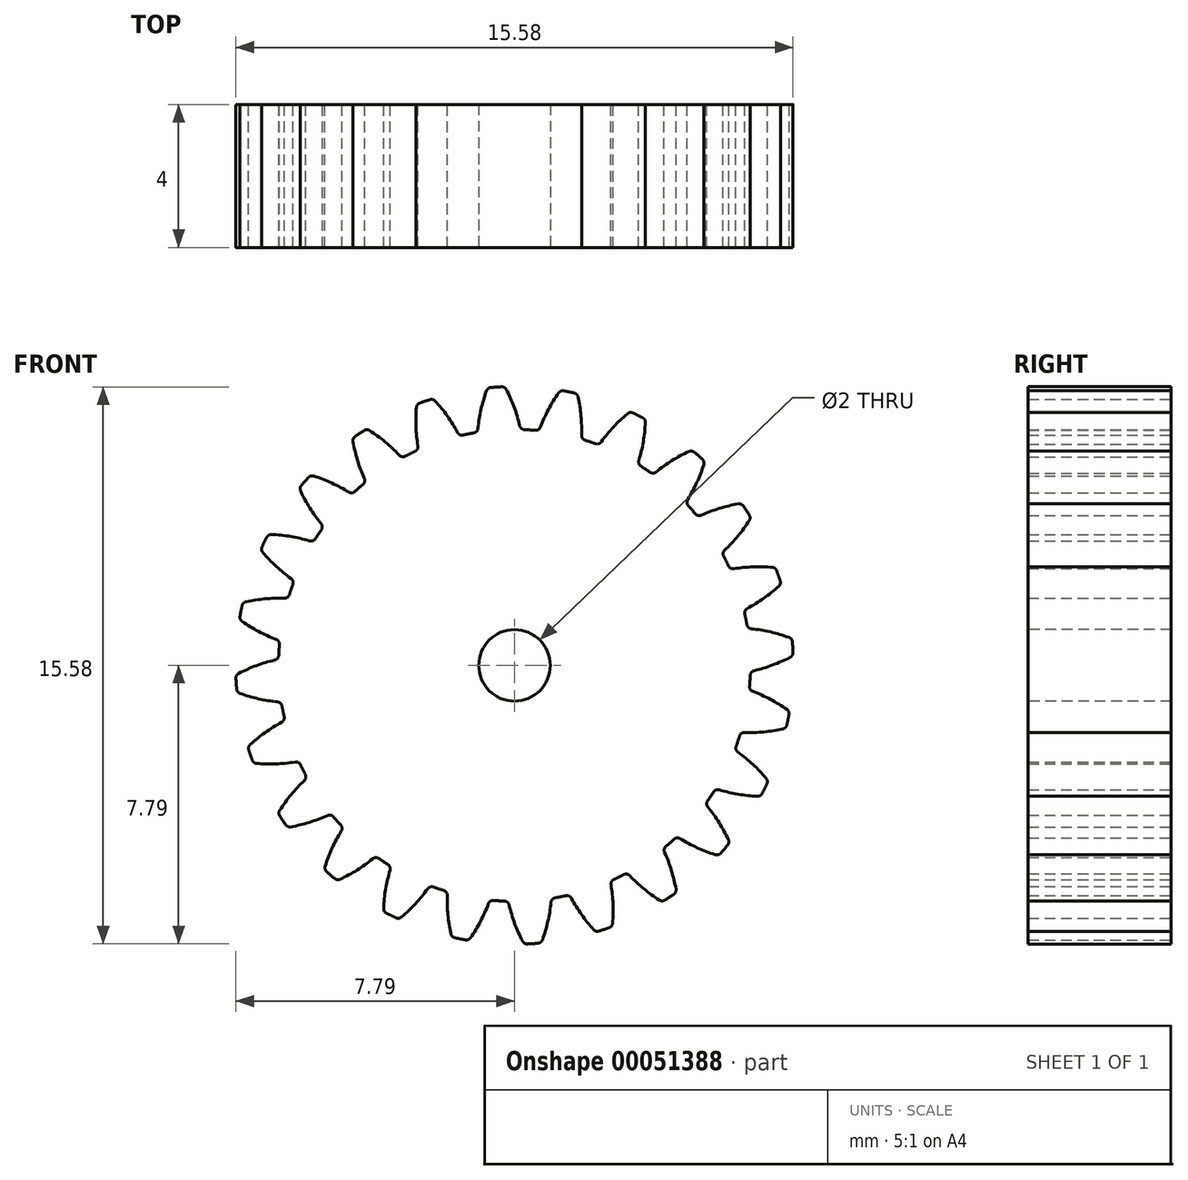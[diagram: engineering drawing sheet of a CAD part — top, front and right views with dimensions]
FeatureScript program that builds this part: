
annotation { "Feature Type Name" : "Feature", "Feature Type Description" : "" }
export const myFeature = defineFeature(function(context is Context, id is Id, definition is map)
    precondition{}
    {
        {
            var Q0;
            Q0=qCreatedBy(makeId("Front.planeOp"),FACE);
            var sketch = newSketch(context, id + "F0", { "sketchPlane" : qUnion([Q0])});
            skCircle(sketch, "E0", {"center": v(0, 0) * mm, "radius": 6.6 * mm, "construction": true});
            skCircle(sketch, "E1", {"center": v(0, 0) * mm, "radius": 7.2 * mm, "construction": true});
            skCircle(sketch, "E2", {"center": v(0, 0) * mm, "radius": 7.8 * mm, "construction": true});
            skLineSegment(sketch, "E3", {"start": v(0, 0) * mm, "end": v(0, 6.31) * mm, "construction": true});
            skCircle(sketch, "E4", {"center": v(0, 7.2) * mm, "radius": 4.32 * mm, "construction": true});
            skCircle(sketch, "E5.cCircle", {"center": v(0, 0) * mm, "radius": 6.31 * mm, "construction": true});
            skLineSegment(sketch, "E5.0", {"start": v(0, 6.31) * mm, "end": v(0.82, 6.26) * mm, "construction": true});
            skLineSegment(sketch, "E5.1", {"start": v(0.82, 6.26) * mm, "end": v(1.63, 6.1) * mm, "construction": true});
            skLineSegment(sketch, "E5.2", {"start": v(1.63, 6.1) * mm, "end": v(2.41, 5.83) * mm, "construction": true});
            skLineSegment(sketch, "E5.3", {"start": v(2.41, 5.83) * mm, "end": v(3.16, 5.46) * mm, "construction": true});
            skLineSegment(sketch, "E5.4", {"start": v(3.16, 5.46) * mm, "end": v(3.84, 5) * mm, "construction": true});
            skLineSegment(sketch, "E5.5", {"start": v(3.84, 5) * mm, "end": v(4.46, 4.46) * mm, "construction": true});
            skLineSegment(sketch, "E5.6", {"start": v(4.46, 4.46) * mm, "end": v(5, 3.84) * mm, "construction": true});
            skLineSegment(sketch, "E5.7", {"start": v(5, 3.84) * mm, "end": v(5.46, 3.16) * mm, "construction": true});
            skLineSegment(sketch, "E5.8", {"start": v(5.46, 3.16) * mm, "end": v(5.83, 2.41) * mm, "construction": true});
            skLineSegment(sketch, "E5.9", {"start": v(5.83, 2.41) * mm, "end": v(6.1, 1.63) * mm, "construction": true});
            skLineSegment(sketch, "E5.10", {"start": v(6.1, 1.63) * mm, "end": v(6.26, 0.82) * mm, "construction": true});
            skLineSegment(sketch, "E5.11", {"start": v(6.26, 0.82) * mm, "end": v(6.31, 0) * mm, "construction": true});
            skLineSegment(sketch, "E5.12", {"start": v(6.31, 0) * mm, "end": v(6.26, -0.82) * mm, "construction": true});
            skLineSegment(sketch, "E5.13", {"start": v(6.26, -0.82) * mm, "end": v(6.1, -1.63) * mm, "construction": true});
            skLineSegment(sketch, "E5.14", {"start": v(6.1, -1.63) * mm, "end": v(5.83, -2.41) * mm, "construction": true});
            skLineSegment(sketch, "E5.15", {"start": v(5.83, -2.41) * mm, "end": v(5.46, -3.16) * mm, "construction": true});
            skLineSegment(sketch, "E5.16", {"start": v(5.46, -3.16) * mm, "end": v(5, -3.84) * mm, "construction": true});
            skLineSegment(sketch, "E5.17", {"start": v(5, -3.84) * mm, "end": v(4.46, -4.46) * mm, "construction": true});
            skLineSegment(sketch, "E5.18", {"start": v(4.46, -4.46) * mm, "end": v(3.84, -5) * mm, "construction": true});
            skLineSegment(sketch, "E5.19", {"start": v(3.84, -5) * mm, "end": v(3.16, -5.46) * mm, "construction": true});
            skLineSegment(sketch, "E5.20", {"start": v(3.16, -5.46) * mm, "end": v(2.41, -5.83) * mm, "construction": true});
            skLineSegment(sketch, "E5.21", {"start": v(2.41, -5.83) * mm, "end": v(1.63, -6.1) * mm, "construction": true});
            skLineSegment(sketch, "E5.22", {"start": v(1.63, -6.1) * mm, "end": v(0.82, -6.26) * mm, "construction": true});
            skLineSegment(sketch, "E5.23", {"start": v(0.82, -6.26) * mm, "end": v(0, -6.31) * mm, "construction": true});
            skLineSegment(sketch, "E5.24", {"start": v(0, -6.31) * mm, "end": v(-0.82, -6.26) * mm, "construction": true});
            skLineSegment(sketch, "E5.25", {"start": v(-0.82, -6.26) * mm, "end": v(-1.63, -6.1) * mm, "construction": true});
            skLineSegment(sketch, "E5.26", {"start": v(-1.63, -6.1) * mm, "end": v(-2.41, -5.83) * mm, "construction": true});
            skLineSegment(sketch, "E5.27", {"start": v(-2.41, -5.83) * mm, "end": v(-3.16, -5.46) * mm, "construction": true});
            skLineSegment(sketch, "E5.28", {"start": v(-3.16, -5.46) * mm, "end": v(-3.84, -5) * mm, "construction": true});
            skLineSegment(sketch, "E5.29", {"start": v(-3.84, -5) * mm, "end": v(-4.46, -4.46) * mm, "construction": true});
            skLineSegment(sketch, "E5.30", {"start": v(-4.46, -4.46) * mm, "end": v(-5, -3.84) * mm, "construction": true});
            skLineSegment(sketch, "E5.31", {"start": v(-5, -3.84) * mm, "end": v(-5.46, -3.16) * mm, "construction": true});
            skLineSegment(sketch, "E5.32", {"start": v(-5.46, -3.16) * mm, "end": v(-5.83, -2.41) * mm, "construction": true});
            skLineSegment(sketch, "E5.33", {"start": v(-5.83, -2.41) * mm, "end": v(-6.1, -1.63) * mm, "construction": true});
            skLineSegment(sketch, "E5.34", {"start": v(-6.1, -1.63) * mm, "end": v(-6.26, -0.82) * mm, "construction": true});
            skLineSegment(sketch, "E5.35", {"start": v(-6.26, -0.82) * mm, "end": v(-6.31, 0) * mm, "construction": true});
            skLineSegment(sketch, "E5.36", {"start": v(-6.31, 0) * mm, "end": v(-6.26, 0.82) * mm, "construction": true});
            skLineSegment(sketch, "E5.37", {"start": v(-6.26, 0.82) * mm, "end": v(-6.1, 1.63) * mm, "construction": true});
            skLineSegment(sketch, "E5.38", {"start": v(-6.1, 1.63) * mm, "end": v(-5.83, 2.41) * mm, "construction": true});
            skLineSegment(sketch, "E5.39", {"start": v(-5.83, 2.41) * mm, "end": v(-5.46, 3.16) * mm, "construction": true});
            skLineSegment(sketch, "E5.40", {"start": v(-5.46, 3.16) * mm, "end": v(-5, 3.84) * mm, "construction": true});
            skLineSegment(sketch, "E5.41", {"start": v(-5, 3.84) * mm, "end": v(-4.46, 4.46) * mm, "construction": true});
            skLineSegment(sketch, "E5.42", {"start": v(-4.46, 4.46) * mm, "end": v(-3.84, 5) * mm, "construction": true});
            skLineSegment(sketch, "E5.43", {"start": v(-3.84, 5) * mm, "end": v(-3.16, 5.46) * mm, "construction": true});
            skLineSegment(sketch, "E5.44", {"start": v(-3.16, 5.46) * mm, "end": v(-2.41, 5.83) * mm, "construction": true});
            skLineSegment(sketch, "E5.45", {"start": v(-2.41, 5.83) * mm, "end": v(-1.63, 6.1) * mm, "construction": true});
            skLineSegment(sketch, "E5.46", {"start": v(-1.63, 6.1) * mm, "end": v(-0.82, 6.26) * mm, "construction": true});
            skLineSegment(sketch, "E5.47", {"start": v(-0.82, 6.26) * mm, "end": v(0, 6.31) * mm, "construction": true});
            skLineSegment(sketch, "E6.0", {"start": v(-0.41, 6.31) * mm, "end": v(0.41, 6.31) * mm});
            skLineSegment(sketch, "E6.1", {"start": v(0.41, 6.31) * mm, "end": v(1.23, 6.2) * mm});
            skLineSegment(sketch, "E6.2", {"start": v(1.23, 6.2) * mm, "end": v(2.03, 5.99) * mm});
            skLineSegment(sketch, "E6.3", {"start": v(2.03, 5.99) * mm, "end": v(2.8, 5.67) * mm});
            skLineSegment(sketch, "E6.4", {"start": v(2.8, 5.67) * mm, "end": v(3.51, 5.26) * mm});
            skLineSegment(sketch, "E6.5", {"start": v(3.51, 5.26) * mm, "end": v(4.17, 4.75) * mm});
            skLineSegment(sketch, "E6.6", {"start": v(4.17, 4.75) * mm, "end": v(4.75, 4.17) * mm});
            skLineSegment(sketch, "E6.7", {"start": v(4.75, 4.17) * mm, "end": v(5.26, 3.51) * mm, "construction": true});
            skLineSegment(sketch, "E6.8", {"start": v(5.26, 3.51) * mm, "end": v(5.67, 2.8) * mm});
            skLineSegment(sketch, "E6.9", {"start": v(5.67, 2.8) * mm, "end": v(5.99, 2.03) * mm});
            skLineSegment(sketch, "E6.10", {"start": v(5.99, 2.03) * mm, "end": v(6.2, 1.23) * mm});
            skLineSegment(sketch, "E6.11", {"start": v(6.2, 1.23) * mm, "end": v(6.31, 0.41) * mm});
            skLineSegment(sketch, "E6.12", {"start": v(6.31, 0.41) * mm, "end": v(6.31, -0.41) * mm});
            skLineSegment(sketch, "E6.13", {"start": v(6.31, -0.41) * mm, "end": v(6.2, -1.23) * mm});
            skLineSegment(sketch, "E6.14", {"start": v(6.2, -1.23) * mm, "end": v(5.99, -2.03) * mm});
            skLineSegment(sketch, "E6.15", {"start": v(5.99, -2.03) * mm, "end": v(5.67, -2.8) * mm});
            skLineSegment(sketch, "E6.16", {"start": v(5.67, -2.8) * mm, "end": v(5.26, -3.51) * mm});
            skLineSegment(sketch, "E6.17", {"start": v(5.26, -3.51) * mm, "end": v(4.75, -4.17) * mm});
            skLineSegment(sketch, "E6.18", {"start": v(4.75, -4.17) * mm, "end": v(4.17, -4.75) * mm});
            skLineSegment(sketch, "E6.19", {"start": v(4.17, -4.75) * mm, "end": v(3.51, -5.26) * mm});
            skLineSegment(sketch, "E6.20", {"start": v(3.51, -5.26) * mm, "end": v(2.8, -5.67) * mm});
            skLineSegment(sketch, "E6.21", {"start": v(2.8, -5.67) * mm, "end": v(2.03, -5.99) * mm});
            skLineSegment(sketch, "E6.22", {"start": v(2.03, -5.99) * mm, "end": v(1.23, -6.2) * mm});
            skLineSegment(sketch, "E6.23", {"start": v(1.23, -6.2) * mm, "end": v(0.41, -6.31) * mm});
            skLineSegment(sketch, "E6.24", {"start": v(0.41, -6.31) * mm, "end": v(-0.41, -6.31) * mm});
            skLineSegment(sketch, "E6.25", {"start": v(-0.41, -6.31) * mm, "end": v(-1.23, -6.2) * mm});
            skLineSegment(sketch, "E6.26", {"start": v(-1.23, -6.2) * mm, "end": v(-2.03, -5.99) * mm});
            skLineSegment(sketch, "E6.27", {"start": v(-2.03, -5.99) * mm, "end": v(-2.8, -5.67) * mm});
            skLineSegment(sketch, "E6.28", {"start": v(-2.8, -5.67) * mm, "end": v(-3.51, -5.26) * mm});
            skLineSegment(sketch, "E6.29", {"start": v(-3.51, -5.26) * mm, "end": v(-4.17, -4.75) * mm});
            skLineSegment(sketch, "E6.30", {"start": v(-4.17, -4.75) * mm, "end": v(-4.75, -4.17) * mm});
            skLineSegment(sketch, "E6.31", {"start": v(-4.75, -4.17) * mm, "end": v(-5.26, -3.51) * mm});
            skLineSegment(sketch, "E6.32", {"start": v(-5.26, -3.51) * mm, "end": v(-5.67, -2.8) * mm});
            skLineSegment(sketch, "E6.33", {"start": v(-5.67, -2.8) * mm, "end": v(-5.99, -2.03) * mm});
            skLineSegment(sketch, "E6.34", {"start": v(-5.99, -2.03) * mm, "end": v(-6.2, -1.23) * mm});
            skLineSegment(sketch, "E6.35", {"start": v(-6.2, -1.23) * mm, "end": v(-6.31, -0.41) * mm});
            skLineSegment(sketch, "E6.36", {"start": v(-6.31, -0.41) * mm, "end": v(-6.31, 0.41) * mm});
            skLineSegment(sketch, "E6.37", {"start": v(-6.31, 0.41) * mm, "end": v(-6.2, 1.23) * mm});
            skLineSegment(sketch, "E6.38", {"start": v(-6.2, 1.23) * mm, "end": v(-5.99, 2.03) * mm});
            skLineSegment(sketch, "E6.39", {"start": v(-5.99, 2.03) * mm, "end": v(-5.67, 2.8) * mm});
            skLineSegment(sketch, "E6.40", {"start": v(-5.67, 2.8) * mm, "end": v(-5.26, 3.51) * mm});
            skLineSegment(sketch, "E6.41", {"start": v(-5.26, 3.51) * mm, "end": v(-4.75, 4.17) * mm});
            skLineSegment(sketch, "E6.42", {"start": v(-4.75, 4.17) * mm, "end": v(-4.17, 4.75) * mm});
            skLineSegment(sketch, "E6.43", {"start": v(-4.17, 4.75) * mm, "end": v(-3.51, 5.26) * mm});
            skLineSegment(sketch, "E6.44", {"start": v(-3.51, 5.26) * mm, "end": v(-2.8, 5.67) * mm});
            skLineSegment(sketch, "E6.45", {"start": v(-2.8, 5.67) * mm, "end": v(-2.03, 5.99) * mm});
            skLineSegment(sketch, "E6.46", {"start": v(-2.03, 5.99) * mm, "end": v(-1.23, 6.2) * mm});
            skLineSegment(sketch, "E6.47", {"start": v(-1.23, 6.2) * mm, "end": v(-0.41, 6.31) * mm});
            skPoint(sketch, "E6.0.midPoint", {"position": v(0, 6.31) * mm});
            skLineSegment(sketch, "E7", {"start": v(0, 7.2) * mm, "end": v(-9.03, 7.2) * mm, "construction": true});
            skLineSegment(sketch, "E8", {"start": v(0, 7.2) * mm, "end": v(-8.97, 3.93) * mm, "construction": true});
            skCircle(sketch, "E9", {"center": v(-4.06, 5.72) * mm, "radius": 4.32 * mm, "construction": true});
            skArc(sketch, "E10", {"start": v(-0.23, 7.71) * mm, "mid": v(0, 7.22) * mm, "end": v(0.15, 6.7) * mm});
            skLineSegment(sketch, "E11", {"start": v(0, 0) * mm, "end": v(-0.41, 6.31) * mm, "construction": true});
            skArc(sketch, "E12.MirrorCS", {"start": v(-0.78, 7.68) * mm, "mid": v(-0.93, 7.16) * mm, "end": v(-1.02, 6.63) * mm});
            skArc(sketch, "E13", {"start": v(-0.66, 7.77) * mm, "mid": v(-0.51, 7.78) * mm, "end": v(-0.36, 7.8) * mm});
            skArc(sketch, "E14", {"start": v(-1.14, 6.5) * mm, "mid": v(0.43, -6.59) * mm, "end": v(0.28, 6.6) * mm});
            skPoint(sketch, "E15.visualSharp", {"position": v(-1.03, 6.52) * mm});
            skArc(sketch, "E15.filletArc", {"start": v(-1.14, 6.5) * mm, "mid": v(-1.06, 6.54) * mm, "end": v(-1.02, 6.63) * mm});
            skPoint(sketch, "E16.visualSharp", {"position": v(0.17, 6.6) * mm});
            skArc(sketch, "E16.filletArc", {"start": v(0.15, 6.7) * mm, "mid": v(0.2, 6.63) * mm, "end": v(0.28, 6.6) * mm});
            skPoint(sketch, "E17.visualSharp", {"position": v(-0.75, 7.76) * mm});
            skArc(sketch, "E17.filletArc", {"start": v(-0.66, 7.77) * mm, "mid": v(-0.74, 7.74) * mm, "end": v(-0.78, 7.68) * mm});
            skPoint(sketch, "E18.visualSharp", {"position": v(-0.27, 7.8) * mm});
            skArc(sketch, "E18.filletArc", {"start": v(-0.23, 7.71) * mm, "mid": v(-0.28, 7.77) * mm, "end": v(-0.36, 7.8) * mm});
            skArc(sketch, "E19.1.0", {"start": v(-2.78, 5.98) * mm, "mid": v(-2.72, 6.05) * mm, "end": v(-2.7, 6.14) * mm});
            skArc(sketch, "E19.1.1", {"start": v(-2.74, 7.21) * mm, "mid": v(-2.76, 6.67) * mm, "end": v(-2.7, 6.14) * mm});
            skArc(sketch, "E19.1.2", {"start": v(-2.65, 7.34) * mm, "mid": v(-2.71, 7.29) * mm, "end": v(-2.74, 7.21) * mm});
            skArc(sketch, "E19.1.3", {"start": v(-2.65, 7.34) * mm, "mid": v(-2.5, 7.39) * mm, "end": v(-2.36, 7.43) * mm});
            skArc(sketch, "E19.1.4", {"start": v(-2.21, 7.4) * mm, "mid": v(-2.28, 7.43) * mm, "end": v(-2.36, 7.43) * mm});
            skArc(sketch, "E19.1.5", {"start": v(-2.21, 7.4) * mm, "mid": v(-1.88, 6.97) * mm, "end": v(-1.6, 6.51) * mm});
            skArc(sketch, "E19.1.6", {"start": v(-1.6, 6.51) * mm, "mid": v(-1.53, 6.45) * mm, "end": v(-1.43, 6.44) * mm});
            skArc(sketch, "E19.2.0", {"start": v(-4.24, 5.06) * mm, "mid": v(-4.19, 5.14) * mm, "end": v(-4.2, 5.23) * mm});
            skArc(sketch, "E19.2.1", {"start": v(-4.52, 6.26) * mm, "mid": v(-4.39, 5.73) * mm, "end": v(-4.2, 5.23) * mm});
            skArc(sketch, "E19.2.2", {"start": v(-4.46, 6.4) * mm, "mid": v(-4.5, 6.34) * mm, "end": v(-4.52, 6.26) * mm});
            skArc(sketch, "E19.2.3", {"start": v(-4.46, 6.4) * mm, "mid": v(-4.33, 6.49) * mm, "end": v(-4.2, 6.57) * mm});
            skArc(sketch, "E19.2.4", {"start": v(-4.05, 6.57) * mm, "mid": v(-4.13, 6.6) * mm, "end": v(-4.2, 6.57) * mm});
            skArc(sketch, "E19.2.5", {"start": v(-4.05, 6.57) * mm, "mid": v(-3.62, 6.25) * mm, "end": v(-3.23, 5.88) * mm});
            skArc(sketch, "E19.2.6", {"start": v(-3.23, 5.88) * mm, "mid": v(-3.14, 5.84) * mm, "end": v(-3.05, 5.85) * mm});
            skArc(sketch, "E19.3.0", {"start": v(-5.4, 3.8) * mm, "mid": v(-5.38, 3.88) * mm, "end": v(-5.4, 3.96) * mm});
            skArc(sketch, "E19.3.1", {"start": v(-5.98, 4.88) * mm, "mid": v(-5.72, 4.4) * mm, "end": v(-5.4, 3.96) * mm});
            skArc(sketch, "E19.3.2", {"start": v(-5.96, 5.03) * mm, "mid": v(-6, 4.96) * mm, "end": v(-5.98, 4.88) * mm});
            skArc(sketch, "E19.3.3", {"start": v(-5.96, 5.03) * mm, "mid": v(-5.86, 5.14) * mm, "end": v(-5.76, 5.25) * mm});
            skArc(sketch, "E19.3.4", {"start": v(-5.61, 5.3) * mm, "mid": v(-5.7, 5.3) * mm, "end": v(-5.76, 5.25) * mm});
            skArc(sketch, "E19.3.5", {"start": v(-5.61, 5.3) * mm, "mid": v(-5.11, 5.1) * mm, "end": v(-4.64, 4.85) * mm});
            skArc(sketch, "E19.3.6", {"start": v(-4.64, 4.85) * mm, "mid": v(-4.55, 4.82) * mm, "end": v(-4.46, 4.86) * mm});
            skArc(sketch, "E19.4.0", {"start": v(-6.2, 2.26) * mm, "mid": v(-6.2, 2.36) * mm, "end": v(-6.25, 2.43) * mm});
            skArc(sketch, "E19.4.1", {"start": v(-7.04, 3.16) * mm, "mid": v(-6.67, 2.77) * mm, "end": v(-6.25, 2.43) * mm});
            skArc(sketch, "E19.4.2", {"start": v(-7.06, 3.31) * mm, "mid": v(-7.07, 3.23) * mm, "end": v(-7.04, 3.16) * mm});
            skArc(sketch, "E19.4.3", {"start": v(-7.06, 3.31) * mm, "mid": v(-7, 3.45) * mm, "end": v(-6.93, 3.58) * mm});
            skArc(sketch, "E19.4.4", {"start": v(-6.8, 3.66) * mm, "mid": v(-6.87, 3.64) * mm, "end": v(-6.93, 3.58) * mm});
            skArc(sketch, "E19.4.5", {"start": v(-6.8, 3.66) * mm, "mid": v(-6.26, 3.6) * mm, "end": v(-5.73, 3.48) * mm});
            skArc(sketch, "E19.4.6", {"start": v(-5.73, 3.48) * mm, "mid": v(-5.64, 3.48) * mm, "end": v(-5.57, 3.54) * mm});
            skArc(sketch, "E19.5.0", {"start": v(-6.57, 0.58) * mm, "mid": v(-6.6, 0.67) * mm, "end": v(-6.67, 0.73) * mm});
            skArc(sketch, "E19.5.1", {"start": v(-7.62, 1.23) * mm, "mid": v(-7.16, 0.95) * mm, "end": v(-6.67, 0.73) * mm});
            skArc(sketch, "E19.5.2", {"start": v(-7.68, 1.37) * mm, "mid": v(-7.67, 1.3) * mm, "end": v(-7.62, 1.23) * mm});
            skArc(sketch, "E19.5.3", {"start": v(-7.68, 1.37) * mm, "mid": v(-7.65, 1.52) * mm, "end": v(-7.62, 1.67) * mm});
            skArc(sketch, "E19.5.4", {"start": v(-7.5, 1.78) * mm, "mid": v(-7.58, 1.74) * mm, "end": v(-7.62, 1.67) * mm});
            skArc(sketch, "E19.5.5", {"start": v(-7.5, 1.78) * mm, "mid": v(-6.98, 1.86) * mm, "end": v(-6.44, 1.88) * mm});
            skArc(sketch, "E19.5.6", {"start": v(-6.44, 1.88) * mm, "mid": v(-6.35, 1.9) * mm, "end": v(-6.3, 1.98) * mm});
            skArc(sketch, "E19.6.0", {"start": v(-6.5, -1.14) * mm, "mid": v(-6.54, -1.06) * mm, "end": v(-6.63, -1.02) * mm});
            skArc(sketch, "E19.6.1", {"start": v(-7.68, -0.78) * mm, "mid": v(-7.16, -0.93) * mm, "end": v(-6.63, -1.02) * mm});
            skArc(sketch, "E19.6.2", {"start": v(-7.77, -0.66) * mm, "mid": v(-7.74, -0.74) * mm, "end": v(-7.68, -0.78) * mm});
            skArc(sketch, "E19.6.3", {"start": v(-7.77, -0.66) * mm, "mid": v(-7.78, -0.51) * mm, "end": v(-7.8, -0.36) * mm});
            skArc(sketch, "E19.6.4", {"start": v(-7.71, -0.23) * mm, "mid": v(-7.77, -0.28) * mm, "end": v(-7.8, -0.36) * mm});
            skArc(sketch, "E19.6.5", {"start": v(-7.71, -0.23) * mm, "mid": v(-7.22, 0) * mm, "end": v(-6.7, 0.15) * mm});
            skArc(sketch, "E19.6.6", {"start": v(-6.7, 0.15) * mm, "mid": v(-6.63, 0.2) * mm, "end": v(-6.6, 0.28) * mm});
            skArc(sketch, "E19.7.0", {"start": v(-5.98, -2.78) * mm, "mid": v(-6.05, -2.72) * mm, "end": v(-6.14, -2.7) * mm});
            skArc(sketch, "E19.7.1", {"start": v(-7.21, -2.74) * mm, "mid": v(-6.67, -2.76) * mm, "end": v(-6.14, -2.7) * mm});
            skArc(sketch, "E19.7.2", {"start": v(-7.34, -2.65) * mm, "mid": v(-7.29, -2.71) * mm, "end": v(-7.21, -2.74) * mm});
            skArc(sketch, "E19.7.3", {"start": v(-7.34, -2.65) * mm, "mid": v(-7.39, -2.5) * mm, "end": v(-7.43, -2.36) * mm});
            skArc(sketch, "E19.7.4", {"start": v(-7.4, -2.21) * mm, "mid": v(-7.43, -2.28) * mm, "end": v(-7.43, -2.36) * mm});
            skArc(sketch, "E19.7.5", {"start": v(-7.4, -2.21) * mm, "mid": v(-6.97, -1.88) * mm, "end": v(-6.51, -1.6) * mm});
            skArc(sketch, "E19.7.6", {"start": v(-6.51, -1.6) * mm, "mid": v(-6.45, -1.53) * mm, "end": v(-6.44, -1.43) * mm});
            skArc(sketch, "E19.8.0", {"start": v(-5.06, -4.24) * mm, "mid": v(-5.14, -4.19) * mm, "end": v(-5.23, -4.2) * mm});
            skArc(sketch, "E19.8.1", {"start": v(-6.26, -4.52) * mm, "mid": v(-5.73, -4.39) * mm, "end": v(-5.23, -4.2) * mm});
            skArc(sketch, "E19.8.2", {"start": v(-6.4, -4.46) * mm, "mid": v(-6.34, -4.5) * mm, "end": v(-6.26, -4.52) * mm});
            skArc(sketch, "E19.8.3", {"start": v(-6.4, -4.46) * mm, "mid": v(-6.49, -4.33) * mm, "end": v(-6.57, -4.2) * mm});
            skArc(sketch, "E19.8.4", {"start": v(-6.57, -4.05) * mm, "mid": v(-6.6, -4.13) * mm, "end": v(-6.57, -4.2) * mm});
            skArc(sketch, "E19.8.5", {"start": v(-6.57, -4.05) * mm, "mid": v(-6.25, -3.62) * mm, "end": v(-5.88, -3.23) * mm});
            skArc(sketch, "E19.8.6", {"start": v(-5.88, -3.23) * mm, "mid": v(-5.84, -3.14) * mm, "end": v(-5.85, -3.05) * mm});
            skArc(sketch, "E19.9.0", {"start": v(-3.8, -5.4) * mm, "mid": v(-3.88, -5.38) * mm, "end": v(-3.96, -5.4) * mm});
            skArc(sketch, "E19.9.1", {"start": v(-4.88, -5.98) * mm, "mid": v(-4.4, -5.72) * mm, "end": v(-3.96, -5.4) * mm});
            skArc(sketch, "E19.9.2", {"start": v(-5.03, -5.96) * mm, "mid": v(-4.96, -6) * mm, "end": v(-4.88, -5.98) * mm});
            skArc(sketch, "E19.9.3", {"start": v(-5.03, -5.96) * mm, "mid": v(-5.14, -5.86) * mm, "end": v(-5.25, -5.76) * mm});
            skArc(sketch, "E19.9.4", {"start": v(-5.3, -5.61) * mm, "mid": v(-5.3, -5.7) * mm, "end": v(-5.25, -5.76) * mm});
            skArc(sketch, "E19.9.5", {"start": v(-5.3, -5.61) * mm, "mid": v(-5.1, -5.11) * mm, "end": v(-4.85, -4.64) * mm});
            skArc(sketch, "E19.9.6", {"start": v(-4.85, -4.64) * mm, "mid": v(-4.82, -4.55) * mm, "end": v(-4.86, -4.46) * mm});
            skArc(sketch, "E19.10.0", {"start": v(-2.26, -6.2) * mm, "mid": v(-2.36, -6.2) * mm, "end": v(-2.43, -6.25) * mm});
            skArc(sketch, "E19.10.1", {"start": v(-3.16, -7.04) * mm, "mid": v(-2.77, -6.67) * mm, "end": v(-2.43, -6.25) * mm});
            skArc(sketch, "E19.10.2", {"start": v(-3.31, -7.06) * mm, "mid": v(-3.23, -7.07) * mm, "end": v(-3.16, -7.04) * mm});
            skArc(sketch, "E19.10.3", {"start": v(-3.31, -7.06) * mm, "mid": v(-3.45, -7) * mm, "end": v(-3.58, -6.93) * mm});
            skArc(sketch, "E19.10.4", {"start": v(-3.66, -6.8) * mm, "mid": v(-3.64, -6.87) * mm, "end": v(-3.58, -6.93) * mm});
            skArc(sketch, "E19.10.5", {"start": v(-3.66, -6.8) * mm, "mid": v(-3.6, -6.26) * mm, "end": v(-3.48, -5.73) * mm});
            skArc(sketch, "E19.10.6", {"start": v(-3.48, -5.73) * mm, "mid": v(-3.48, -5.64) * mm, "end": v(-3.54, -5.57) * mm});
            skArc(sketch, "E19.11.0", {"start": v(-0.58, -6.57) * mm, "mid": v(-0.67, -6.6) * mm, "end": v(-0.73, -6.67) * mm});
            skArc(sketch, "E19.11.1", {"start": v(-1.23, -7.62) * mm, "mid": v(-0.95, -7.16) * mm, "end": v(-0.73, -6.67) * mm});
            skArc(sketch, "E19.11.2", {"start": v(-1.37, -7.68) * mm, "mid": v(-1.3, -7.67) * mm, "end": v(-1.23, -7.62) * mm});
            skArc(sketch, "E19.11.3", {"start": v(-1.37, -7.68) * mm, "mid": v(-1.52, -7.65) * mm, "end": v(-1.67, -7.62) * mm});
            skArc(sketch, "E19.11.4", {"start": v(-1.78, -7.5) * mm, "mid": v(-1.74, -7.58) * mm, "end": v(-1.67, -7.62) * mm});
            skArc(sketch, "E19.11.5", {"start": v(-1.78, -7.5) * mm, "mid": v(-1.86, -6.98) * mm, "end": v(-1.88, -6.44) * mm});
            skArc(sketch, "E19.11.6", {"start": v(-1.88, -6.44) * mm, "mid": v(-1.9, -6.35) * mm, "end": v(-1.98, -6.3) * mm});
            skArc(sketch, "E19.12.0", {"start": v(1.14, -6.5) * mm, "mid": v(1.06, -6.54) * mm, "end": v(1.02, -6.63) * mm});
            skArc(sketch, "E19.12.1", {"start": v(0.78, -7.68) * mm, "mid": v(0.93, -7.16) * mm, "end": v(1.02, -6.63) * mm});
            skArc(sketch, "E19.12.2", {"start": v(0.66, -7.77) * mm, "mid": v(0.74, -7.74) * mm, "end": v(0.78, -7.68) * mm});
            skArc(sketch, "E19.12.3", {"start": v(0.66, -7.77) * mm, "mid": v(0.51, -7.78) * mm, "end": v(0.36, -7.8) * mm});
            skArc(sketch, "E19.12.4", {"start": v(0.23, -7.71) * mm, "mid": v(0.28, -7.77) * mm, "end": v(0.36, -7.8) * mm});
            skArc(sketch, "E19.12.5", {"start": v(0.23, -7.71) * mm, "mid": v(0, -7.22) * mm, "end": v(-0.15, -6.7) * mm});
            skArc(sketch, "E19.12.6", {"start": v(-0.15, -6.7) * mm, "mid": v(-0.2, -6.63) * mm, "end": v(-0.28, -6.6) * mm});
            skArc(sketch, "E19.13.0", {"start": v(2.78, -5.98) * mm, "mid": v(2.72, -6.05) * mm, "end": v(2.7, -6.14) * mm});
            skArc(sketch, "E19.13.1", {"start": v(2.74, -7.21) * mm, "mid": v(2.76, -6.67) * mm, "end": v(2.7, -6.14) * mm});
            skArc(sketch, "E19.13.2", {"start": v(2.65, -7.34) * mm, "mid": v(2.71, -7.29) * mm, "end": v(2.74, -7.21) * mm});
            skArc(sketch, "E19.13.3", {"start": v(2.65, -7.34) * mm, "mid": v(2.5, -7.39) * mm, "end": v(2.36, -7.43) * mm});
            skArc(sketch, "E19.13.4", {"start": v(2.21, -7.4) * mm, "mid": v(2.28, -7.43) * mm, "end": v(2.36, -7.43) * mm});
            skArc(sketch, "E19.13.5", {"start": v(2.21, -7.4) * mm, "mid": v(1.88, -6.97) * mm, "end": v(1.6, -6.51) * mm});
            skArc(sketch, "E19.13.6", {"start": v(1.6, -6.51) * mm, "mid": v(1.53, -6.45) * mm, "end": v(1.43, -6.44) * mm});
            skArc(sketch, "E19.14.0", {"start": v(4.24, -5.06) * mm, "mid": v(4.19, -5.14) * mm, "end": v(4.2, -5.23) * mm});
            skArc(sketch, "E19.14.1", {"start": v(4.52, -6.26) * mm, "mid": v(4.39, -5.73) * mm, "end": v(4.2, -5.23) * mm});
            skArc(sketch, "E19.14.2", {"start": v(4.46, -6.4) * mm, "mid": v(4.5, -6.34) * mm, "end": v(4.52, -6.26) * mm});
            skArc(sketch, "E19.14.3", {"start": v(4.46, -6.4) * mm, "mid": v(4.33, -6.49) * mm, "end": v(4.2, -6.57) * mm});
            skArc(sketch, "E19.14.4", {"start": v(4.05, -6.57) * mm, "mid": v(4.13, -6.6) * mm, "end": v(4.2, -6.57) * mm});
            skArc(sketch, "E19.14.5", {"start": v(4.05, -6.57) * mm, "mid": v(3.62, -6.25) * mm, "end": v(3.23, -5.88) * mm});
            skArc(sketch, "E19.14.6", {"start": v(3.23, -5.88) * mm, "mid": v(3.14, -5.84) * mm, "end": v(3.05, -5.85) * mm});
            skArc(sketch, "E19.15.0", {"start": v(5.4, -3.8) * mm, "mid": v(5.38, -3.88) * mm, "end": v(5.4, -3.96) * mm});
            skArc(sketch, "E19.15.1", {"start": v(5.98, -4.88) * mm, "mid": v(5.72, -4.4) * mm, "end": v(5.4, -3.96) * mm});
            skArc(sketch, "E19.15.2", {"start": v(5.96, -5.03) * mm, "mid": v(6, -4.96) * mm, "end": v(5.98, -4.88) * mm});
            skArc(sketch, "E19.15.3", {"start": v(5.96, -5.03) * mm, "mid": v(5.86, -5.14) * mm, "end": v(5.76, -5.25) * mm});
            skArc(sketch, "E19.15.4", {"start": v(5.61, -5.3) * mm, "mid": v(5.7, -5.3) * mm, "end": v(5.76, -5.25) * mm});
            skArc(sketch, "E19.15.5", {"start": v(5.61, -5.3) * mm, "mid": v(5.11, -5.1) * mm, "end": v(4.64, -4.85) * mm});
            skArc(sketch, "E19.15.6", {"start": v(4.64, -4.85) * mm, "mid": v(4.55, -4.82) * mm, "end": v(4.46, -4.86) * mm});
            skArc(sketch, "E19.16.0", {"start": v(6.2, -2.26) * mm, "mid": v(6.2, -2.36) * mm, "end": v(6.25, -2.43) * mm});
            skArc(sketch, "E19.16.1", {"start": v(7.04, -3.16) * mm, "mid": v(6.67, -2.77) * mm, "end": v(6.25, -2.43) * mm});
            skArc(sketch, "E19.16.2", {"start": v(7.06, -3.31) * mm, "mid": v(7.07, -3.23) * mm, "end": v(7.04, -3.16) * mm});
            skArc(sketch, "E19.16.3", {"start": v(7.06, -3.31) * mm, "mid": v(7, -3.45) * mm, "end": v(6.93, -3.58) * mm});
            skArc(sketch, "E19.16.4", {"start": v(6.8, -3.66) * mm, "mid": v(6.87, -3.64) * mm, "end": v(6.93, -3.58) * mm});
            skArc(sketch, "E19.16.5", {"start": v(6.8, -3.66) * mm, "mid": v(6.26, -3.6) * mm, "end": v(5.73, -3.48) * mm});
            skArc(sketch, "E19.16.6", {"start": v(5.73, -3.48) * mm, "mid": v(5.64, -3.48) * mm, "end": v(5.57, -3.54) * mm});
            skArc(sketch, "E19.17.0", {"start": v(6.57, -0.58) * mm, "mid": v(6.6, -0.67) * mm, "end": v(6.67, -0.73) * mm});
            skArc(sketch, "E19.17.1", {"start": v(7.62, -1.23) * mm, "mid": v(7.16, -0.95) * mm, "end": v(6.67, -0.73) * mm});
            skArc(sketch, "E19.17.2", {"start": v(7.68, -1.37) * mm, "mid": v(7.67, -1.3) * mm, "end": v(7.62, -1.23) * mm});
            skArc(sketch, "E19.17.3", {"start": v(7.68, -1.37) * mm, "mid": v(7.65, -1.52) * mm, "end": v(7.62, -1.67) * mm});
            skArc(sketch, "E19.17.4", {"start": v(7.5, -1.78) * mm, "mid": v(7.58, -1.74) * mm, "end": v(7.62, -1.67) * mm});
            skArc(sketch, "E19.17.5", {"start": v(7.5, -1.78) * mm, "mid": v(6.98, -1.86) * mm, "end": v(6.44, -1.88) * mm});
            skArc(sketch, "E19.17.6", {"start": v(6.44, -1.88) * mm, "mid": v(6.35, -1.9) * mm, "end": v(6.3, -1.98) * mm});
            skArc(sketch, "E19.18.0", {"start": v(6.5, 1.14) * mm, "mid": v(6.54, 1.06) * mm, "end": v(6.63, 1.02) * mm});
            skArc(sketch, "E19.18.1", {"start": v(7.68, 0.78) * mm, "mid": v(7.16, 0.93) * mm, "end": v(6.63, 1.02) * mm});
            skArc(sketch, "E19.18.2", {"start": v(7.77, 0.66) * mm, "mid": v(7.74, 0.74) * mm, "end": v(7.68, 0.78) * mm});
            skArc(sketch, "E19.18.3", {"start": v(7.77, 0.66) * mm, "mid": v(7.78, 0.51) * mm, "end": v(7.8, 0.36) * mm});
            skArc(sketch, "E19.18.4", {"start": v(7.71, 0.23) * mm, "mid": v(7.77, 0.28) * mm, "end": v(7.8, 0.36) * mm});
            skArc(sketch, "E19.18.5", {"start": v(7.71, 0.23) * mm, "mid": v(7.22, 0) * mm, "end": v(6.7, -0.15) * mm});
            skArc(sketch, "E19.18.6", {"start": v(6.7, -0.15) * mm, "mid": v(6.63, -0.2) * mm, "end": v(6.6, -0.28) * mm});
            skArc(sketch, "E19.19.0", {"start": v(5.98, 2.78) * mm, "mid": v(6.05, 2.72) * mm, "end": v(6.14, 2.7) * mm});
            skArc(sketch, "E19.19.1", {"start": v(7.21, 2.74) * mm, "mid": v(6.67, 2.76) * mm, "end": v(6.14, 2.7) * mm});
            skArc(sketch, "E19.19.2", {"start": v(7.34, 2.65) * mm, "mid": v(7.29, 2.71) * mm, "end": v(7.21, 2.74) * mm});
            skArc(sketch, "E19.19.3", {"start": v(7.34, 2.65) * mm, "mid": v(7.39, 2.5) * mm, "end": v(7.43, 2.36) * mm});
            skArc(sketch, "E19.19.4", {"start": v(7.4, 2.21) * mm, "mid": v(7.43, 2.28) * mm, "end": v(7.43, 2.36) * mm});
            skArc(sketch, "E19.19.5", {"start": v(7.4, 2.21) * mm, "mid": v(6.97, 1.88) * mm, "end": v(6.51, 1.6) * mm});
            skArc(sketch, "E19.19.6", {"start": v(6.51, 1.6) * mm, "mid": v(6.45, 1.53) * mm, "end": v(6.44, 1.43) * mm});
            skArc(sketch, "E19.20.0", {"start": v(5.06, 4.24) * mm, "mid": v(5.14, 4.19) * mm, "end": v(5.23, 4.2) * mm});
            skArc(sketch, "E19.20.1", {"start": v(6.26, 4.52) * mm, "mid": v(5.73, 4.39) * mm, "end": v(5.23, 4.2) * mm});
            skArc(sketch, "E19.20.2", {"start": v(6.4, 4.46) * mm, "mid": v(6.34, 4.5) * mm, "end": v(6.26, 4.52) * mm});
            skArc(sketch, "E19.20.3", {"start": v(6.4, 4.46) * mm, "mid": v(6.49, 4.33) * mm, "end": v(6.57, 4.2) * mm});
            skArc(sketch, "E19.20.4", {"start": v(6.57, 4.05) * mm, "mid": v(6.6, 4.13) * mm, "end": v(6.57, 4.2) * mm});
            skArc(sketch, "E19.20.5", {"start": v(6.57, 4.05) * mm, "mid": v(6.25, 3.62) * mm, "end": v(5.88, 3.23) * mm});
            skArc(sketch, "E19.20.6", {"start": v(5.88, 3.23) * mm, "mid": v(5.84, 3.14) * mm, "end": v(5.85, 3.05) * mm});
            skArc(sketch, "E19.21.0", {"start": v(3.8, 5.4) * mm, "mid": v(3.88, 5.38) * mm, "end": v(3.96, 5.4) * mm});
            skArc(sketch, "E19.21.1", {"start": v(4.88, 5.98) * mm, "mid": v(4.4, 5.72) * mm, "end": v(3.96, 5.4) * mm});
            skArc(sketch, "E19.21.2", {"start": v(5.03, 5.96) * mm, "mid": v(4.96, 6) * mm, "end": v(4.88, 5.98) * mm});
            skArc(sketch, "E19.21.3", {"start": v(5.03, 5.96) * mm, "mid": v(5.14, 5.86) * mm, "end": v(5.25, 5.76) * mm});
            skArc(sketch, "E19.21.4", {"start": v(5.3, 5.61) * mm, "mid": v(5.3, 5.7) * mm, "end": v(5.25, 5.76) * mm});
            skArc(sketch, "E19.21.5", {"start": v(5.3, 5.61) * mm, "mid": v(5.1, 5.11) * mm, "end": v(4.85, 4.64) * mm});
            skArc(sketch, "E19.21.6", {"start": v(4.85, 4.64) * mm, "mid": v(4.82, 4.55) * mm, "end": v(4.86, 4.46) * mm});
            skArc(sketch, "E19.22.0", {"start": v(2.26, 6.2) * mm, "mid": v(2.36, 6.2) * mm, "end": v(2.43, 6.25) * mm});
            skArc(sketch, "E19.22.1", {"start": v(3.16, 7.04) * mm, "mid": v(2.77, 6.67) * mm, "end": v(2.43, 6.25) * mm});
            skArc(sketch, "E19.22.2", {"start": v(3.31, 7.06) * mm, "mid": v(3.23, 7.07) * mm, "end": v(3.16, 7.04) * mm});
            skArc(sketch, "E19.22.3", {"start": v(3.31, 7.06) * mm, "mid": v(3.45, 7) * mm, "end": v(3.58, 6.93) * mm});
            skArc(sketch, "E19.22.4", {"start": v(3.66, 6.8) * mm, "mid": v(3.64, 6.87) * mm, "end": v(3.58, 6.93) * mm});
            skArc(sketch, "E19.22.5", {"start": v(3.66, 6.8) * mm, "mid": v(3.6, 6.26) * mm, "end": v(3.48, 5.73) * mm});
            skArc(sketch, "E19.22.6", {"start": v(3.48, 5.73) * mm, "mid": v(3.48, 5.64) * mm, "end": v(3.54, 5.57) * mm});
            skArc(sketch, "E19.23.0", {"start": v(0.58, 6.57) * mm, "mid": v(0.67, 6.6) * mm, "end": v(0.73, 6.67) * mm});
            skArc(sketch, "E19.23.1", {"start": v(1.23, 7.62) * mm, "mid": v(0.95, 7.16) * mm, "end": v(0.73, 6.67) * mm});
            skArc(sketch, "E19.23.2", {"start": v(1.37, 7.68) * mm, "mid": v(1.3, 7.67) * mm, "end": v(1.23, 7.62) * mm});
            skArc(sketch, "E19.23.3", {"start": v(1.37, 7.68) * mm, "mid": v(1.52, 7.65) * mm, "end": v(1.67, 7.62) * mm});
            skArc(sketch, "E19.23.4", {"start": v(1.78, 7.5) * mm, "mid": v(1.74, 7.58) * mm, "end": v(1.67, 7.62) * mm});
            skArc(sketch, "E19.23.5", {"start": v(1.78, 7.5) * mm, "mid": v(1.86, 6.98) * mm, "end": v(1.88, 6.44) * mm});
            skArc(sketch, "E19.23.6", {"start": v(1.88, 6.44) * mm, "mid": v(1.9, 6.35) * mm, "end": v(1.98, 6.3) * mm});
            skSolve(sketch);
        }
        {
            var Q0;
            Q0 = qSketchRegion(id + "F0", true);
            extrude(context, id + "F1", {"entities" : qUnion([Q0]), "depth" : 4 * mm});
        }
        {
            var Q0;
            Q0=makeQuery(id+"F1.opExtrude","CAP_FACE",FACE,{"disambiguationData":[OSD([sQuery(id+"F0.wireOp",EDGE,"E10"),sQuery(id+"F0.wireOp",EDGE,"E12.MirrorCS"),sQuery(id+"F0.wireOp",EDGE,"E13"),sQuery(id+"F0.wireOp",EDGE,"E14"),sQuery(id+"F0.wireOp",EDGE,"E15.filletArc"),sQuery(id+"F0.wireOp",EDGE,"E16.filletArc"),sQuery(id+"F0.wireOp",EDGE,"E17.filletArc"),sQuery(id+"F0.wireOp",EDGE,"E18.filletArc"),sQuery(id+"F0.wireOp",EDGE,"E19.1.0"),sQuery(id+"F0.wireOp",EDGE,"E19.1.1"),sQuery(id+"F0.wireOp",EDGE,"E19.1.2"),sQuery(id+"F0.wireOp",EDGE,"E19.1.3"),sQuery(id+"F0.wireOp",EDGE,"E19.1.4"),sQuery(id+"F0.wireOp",EDGE,"E19.1.5"),sQuery(id+"F0.wireOp",EDGE,"E19.1.6"),sQuery(id+"F0.wireOp",EDGE,"E19.2.0"),sQuery(id+"F0.wireOp",EDGE,"E19.2.1"),sQuery(id+"F0.wireOp",EDGE,"E19.2.2"),sQuery(id+"F0.wireOp",EDGE,"E19.2.3"),sQuery(id+"F0.wireOp",EDGE,"E19.2.4"),sQuery(id+"F0.wireOp",EDGE,"E19.2.5"),sQuery(id+"F0.wireOp",EDGE,"E19.2.6"),sQuery(id+"F0.wireOp",EDGE,"E19.3.0"),sQuery(id+"F0.wireOp",EDGE,"E19.3.1"),sQuery(id+"F0.wireOp",EDGE,"E19.3.2"),sQuery(id+"F0.wireOp",EDGE,"E19.3.3"),sQuery(id+"F0.wireOp",EDGE,"E19.3.4"),sQuery(id+"F0.wireOp",EDGE,"E19.3.5"),sQuery(id+"F0.wireOp",EDGE,"E19.3.6"),sQuery(id+"F0.wireOp",EDGE,"E19.4.0"),sQuery(id+"F0.wireOp",EDGE,"E19.4.1"),sQuery(id+"F0.wireOp",EDGE,"E19.4.2"),sQuery(id+"F0.wireOp",EDGE,"E19.4.3"),sQuery(id+"F0.wireOp",EDGE,"E19.4.4"),sQuery(id+"F0.wireOp",EDGE,"E19.4.5"),sQuery(id+"F0.wireOp",EDGE,"E19.4.6"),sQuery(id+"F0.wireOp",EDGE,"E19.5.0"),sQuery(id+"F0.wireOp",EDGE,"E19.5.1"),sQuery(id+"F0.wireOp",EDGE,"E19.5.2"),sQuery(id+"F0.wireOp",EDGE,"E19.5.3"),sQuery(id+"F0.wireOp",EDGE,"E19.5.4"),sQuery(id+"F0.wireOp",EDGE,"E19.5.5"),sQuery(id+"F0.wireOp",EDGE,"E19.5.6"),sQuery(id+"F0.wireOp",EDGE,"E19.6.0"),sQuery(id+"F0.wireOp",EDGE,"E19.6.1"),sQuery(id+"F0.wireOp",EDGE,"E19.6.2"),sQuery(id+"F0.wireOp",EDGE,"E19.6.3"),sQuery(id+"F0.wireOp",EDGE,"E19.6.4"),sQuery(id+"F0.wireOp",EDGE,"E19.6.5"),sQuery(id+"F0.wireOp",EDGE,"E19.6.6"),sQuery(id+"F0.wireOp",EDGE,"E19.7.0"),sQuery(id+"F0.wireOp",EDGE,"E19.7.1"),sQuery(id+"F0.wireOp",EDGE,"E19.7.2"),sQuery(id+"F0.wireOp",EDGE,"E19.7.3"),sQuery(id+"F0.wireOp",EDGE,"E19.7.4"),sQuery(id+"F0.wireOp",EDGE,"E19.7.5"),sQuery(id+"F0.wireOp",EDGE,"E19.7.6"),sQuery(id+"F0.wireOp",EDGE,"E19.8.0"),sQuery(id+"F0.wireOp",EDGE,"E19.8.1"),sQuery(id+"F0.wireOp",EDGE,"E19.8.2"),sQuery(id+"F0.wireOp",EDGE,"E19.8.3"),sQuery(id+"F0.wireOp",EDGE,"E19.8.4"),sQuery(id+"F0.wireOp",EDGE,"E19.8.5"),sQuery(id+"F0.wireOp",EDGE,"E19.8.6"),sQuery(id+"F0.wireOp",EDGE,"E19.9.0"),sQuery(id+"F0.wireOp",EDGE,"E19.9.1"),sQuery(id+"F0.wireOp",EDGE,"E19.9.2"),sQuery(id+"F0.wireOp",EDGE,"E19.9.3"),sQuery(id+"F0.wireOp",EDGE,"E19.9.4"),sQuery(id+"F0.wireOp",EDGE,"E19.9.5"),sQuery(id+"F0.wireOp",EDGE,"E19.9.6"),sQuery(id+"F0.wireOp",EDGE,"E19.10.0"),sQuery(id+"F0.wireOp",EDGE,"E19.10.1"),sQuery(id+"F0.wireOp",EDGE,"E19.10.2"),sQuery(id+"F0.wireOp",EDGE,"E19.10.3"),sQuery(id+"F0.wireOp",EDGE,"E19.10.4"),sQuery(id+"F0.wireOp",EDGE,"E19.10.5"),sQuery(id+"F0.wireOp",EDGE,"E19.10.6"),sQuery(id+"F0.wireOp",EDGE,"E19.11.0"),sQuery(id+"F0.wireOp",EDGE,"E19.11.1"),sQuery(id+"F0.wireOp",EDGE,"E19.11.2"),sQuery(id+"F0.wireOp",EDGE,"E19.11.3"),sQuery(id+"F0.wireOp",EDGE,"E19.11.4"),sQuery(id+"F0.wireOp",EDGE,"E19.11.5"),sQuery(id+"F0.wireOp",EDGE,"E19.11.6"),sQuery(id+"F0.wireOp",EDGE,"E19.12.0"),sQuery(id+"F0.wireOp",EDGE,"E19.12.1"),sQuery(id+"F0.wireOp",EDGE,"E19.12.2"),sQuery(id+"F0.wireOp",EDGE,"E19.12.3"),sQuery(id+"F0.wireOp",EDGE,"E19.12.4"),sQuery(id+"F0.wireOp",EDGE,"E19.12.5"),sQuery(id+"F0.wireOp",EDGE,"E19.12.6"),sQuery(id+"F0.wireOp",EDGE,"E19.13.0"),sQuery(id+"F0.wireOp",EDGE,"E19.13.1"),sQuery(id+"F0.wireOp",EDGE,"E19.13.2"),sQuery(id+"F0.wireOp",EDGE,"E19.13.3"),sQuery(id+"F0.wireOp",EDGE,"E19.13.4"),sQuery(id+"F0.wireOp",EDGE,"E19.13.5"),sQuery(id+"F0.wireOp",EDGE,"E19.13.6"),sQuery(id+"F0.wireOp",EDGE,"E19.14.0"),sQuery(id+"F0.wireOp",EDGE,"E19.14.1"),sQuery(id+"F0.wireOp",EDGE,"E19.14.2"),sQuery(id+"F0.wireOp",EDGE,"E19.14.3"),sQuery(id+"F0.wireOp",EDGE,"E19.14.4"),sQuery(id+"F0.wireOp",EDGE,"E19.14.5"),sQuery(id+"F0.wireOp",EDGE,"E19.14.6"),sQuery(id+"F0.wireOp",EDGE,"E19.15.0"),sQuery(id+"F0.wireOp",EDGE,"E19.15.1"),sQuery(id+"F0.wireOp",EDGE,"E19.15.2"),sQuery(id+"F0.wireOp",EDGE,"E19.15.3"),sQuery(id+"F0.wireOp",EDGE,"E19.15.4"),sQuery(id+"F0.wireOp",EDGE,"E19.15.5"),sQuery(id+"F0.wireOp",EDGE,"E19.15.6"),sQuery(id+"F0.wireOp",EDGE,"E19.16.0"),sQuery(id+"F0.wireOp",EDGE,"E19.16.1"),sQuery(id+"F0.wireOp",EDGE,"E19.16.2"),sQuery(id+"F0.wireOp",EDGE,"E19.16.3"),sQuery(id+"F0.wireOp",EDGE,"E19.16.4"),sQuery(id+"F0.wireOp",EDGE,"E19.16.5"),sQuery(id+"F0.wireOp",EDGE,"E19.16.6"),sQuery(id+"F0.wireOp",EDGE,"E19.17.0"),sQuery(id+"F0.wireOp",EDGE,"E19.17.1"),sQuery(id+"F0.wireOp",EDGE,"E19.17.2"),sQuery(id+"F0.wireOp",EDGE,"E19.17.3"),sQuery(id+"F0.wireOp",EDGE,"E19.17.4"),sQuery(id+"F0.wireOp",EDGE,"E19.17.5"),sQuery(id+"F0.wireOp",EDGE,"E19.17.6"),sQuery(id+"F0.wireOp",EDGE,"E19.18.0"),sQuery(id+"F0.wireOp",EDGE,"E19.18.1"),sQuery(id+"F0.wireOp",EDGE,"E19.18.2"),sQuery(id+"F0.wireOp",EDGE,"E19.18.3"),sQuery(id+"F0.wireOp",EDGE,"E19.18.4"),sQuery(id+"F0.wireOp",EDGE,"E19.18.5"),sQuery(id+"F0.wireOp",EDGE,"E19.18.6"),sQuery(id+"F0.wireOp",EDGE,"E19.19.0"),sQuery(id+"F0.wireOp",EDGE,"E19.19.1"),sQuery(id+"F0.wireOp",EDGE,"E19.19.2"),sQuery(id+"F0.wireOp",EDGE,"E19.19.3"),sQuery(id+"F0.wireOp",EDGE,"E19.19.4"),sQuery(id+"F0.wireOp",EDGE,"E19.19.5"),sQuery(id+"F0.wireOp",EDGE,"E19.19.6"),sQuery(id+"F0.wireOp",EDGE,"E19.20.0"),sQuery(id+"F0.wireOp",EDGE,"E19.20.1"),sQuery(id+"F0.wireOp",EDGE,"E19.20.2"),sQuery(id+"F0.wireOp",EDGE,"E19.20.3"),sQuery(id+"F0.wireOp",EDGE,"E19.20.4"),sQuery(id+"F0.wireOp",EDGE,"E19.20.5"),sQuery(id+"F0.wireOp",EDGE,"E19.20.6"),sQuery(id+"F0.wireOp",EDGE,"E19.21.0"),sQuery(id+"F0.wireOp",EDGE,"E19.21.1"),sQuery(id+"F0.wireOp",EDGE,"E19.21.2"),sQuery(id+"F0.wireOp",EDGE,"E19.21.3"),sQuery(id+"F0.wireOp",EDGE,"E19.21.4"),sQuery(id+"F0.wireOp",EDGE,"E19.21.5"),sQuery(id+"F0.wireOp",EDGE,"E19.21.6"),sQuery(id+"F0.wireOp",EDGE,"E19.22.0"),sQuery(id+"F0.wireOp",EDGE,"E19.22.1"),sQuery(id+"F0.wireOp",EDGE,"E19.22.2"),sQuery(id+"F0.wireOp",EDGE,"E19.22.3"),sQuery(id+"F0.wireOp",EDGE,"E19.22.4"),sQuery(id+"F0.wireOp",EDGE,"E19.22.5"),sQuery(id+"F0.wireOp",EDGE,"E19.22.6"),sQuery(id+"F0.wireOp",EDGE,"E19.23.0"),sQuery(id+"F0.wireOp",EDGE,"E19.23.1"),sQuery(id+"F0.wireOp",EDGE,"E19.23.2"),sQuery(id+"F0.wireOp",EDGE,"E19.23.3"),sQuery(id+"F0.wireOp",EDGE,"E19.23.4"),sQuery(id+"F0.wireOp",EDGE,"E19.23.5"),sQuery(id+"F0.wireOp",EDGE,"E19.23.6")])],"isStart":false});
            var sketch = newSketch(context, id + "F2", { "sketchPlane" : qUnion([Q0])});
            skCircle(sketch, "E20", {"center": v(0, 0) * mm, "radius": 1 * mm});
            skSolve(sketch);
        }
        {
            var Q0;
            Q0 = qSketchRegion(id + "F2", true);
            extrude(context, id + "F3", {"entities" : qUnion([Q0]), "operationType" : NewBodyOperationType.REMOVE, "oppositeDirection" : true, "depth" : 25 * mm});
        }
    });
